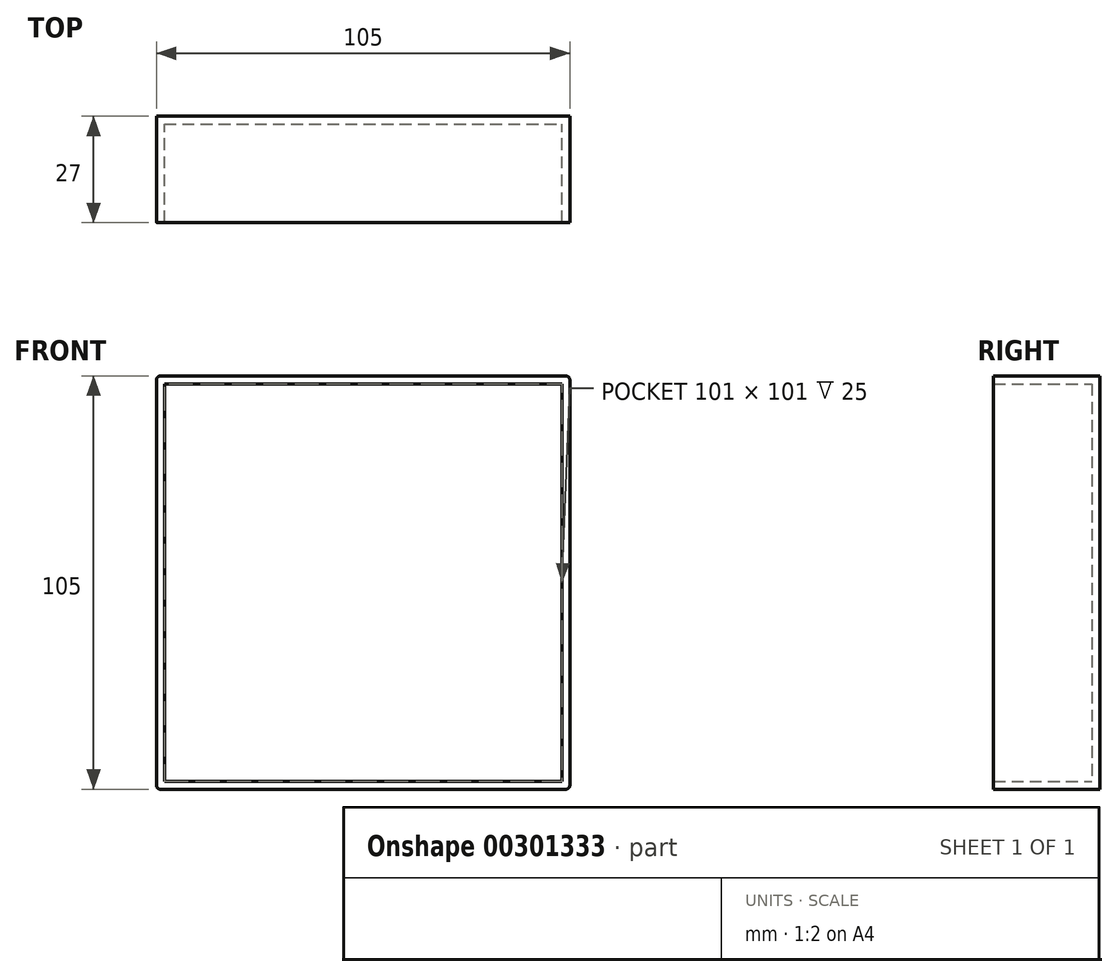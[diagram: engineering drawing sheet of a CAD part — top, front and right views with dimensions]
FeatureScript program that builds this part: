
annotation { "Feature Type Name" : "Feature", "Feature Type Description" : "" }
export const myFeature = defineFeature(function(context is Context, id is Id, definition is map)
    precondition{}
    {
        {
            var Q0;
            Q0=qCreatedBy(makeId("Front.planeOp"),FACE);
            var sketch = newSketch(context, id + "F0", { "sketchPlane" : qUnion([Q0])});
            skLineSegment(sketch, "E0.bottom", {"start": v(-37.92, 57.9) * mm, "end": v(67.08, 57.9) * mm});
            skLineSegment(sketch, "E0.top", {"start": v(-37.92, -47.1) * mm, "end": v(67.08, -47.1) * mm});
            skLineSegment(sketch, "E0.left", {"start": v(-37.92, 57.9) * mm, "end": v(-37.92, -47.1) * mm});
            skLineSegment(sketch, "E0.right", {"start": v(67.08, 57.9) * mm, "end": v(67.08, -47.1) * mm});
            skSolve(sketch);
        }
        {
            var Q0;
            Q0=makeQuery(id+"F0.imprint","IMPRINT",FACE,{"disambiguationData":[TD([[makeQuery(id+"F0.imprint","IMPRINT",EDGE,{"derivedFrom":sQuery(id+"F0.wireOp",EDGE,"E0.bottom")}),-1.0]])]});
            extrude(context, id + "F1", {"entities" : qUnion([Q0]), "depth" : 27 * mm});
        }
        {
            var Q0;
            Q0=makeQuery(id+"F1.opExtrude","CAP_FACE",FACE,{"disambiguationData":[OSD([sQuery(id+"F0.wireOp",EDGE,"E0.bottom"),sQuery(id+"F0.wireOp",EDGE,"E0.top"),sQuery(id+"F0.wireOp",EDGE,"E0.left"),sQuery(id+"F0.wireOp",EDGE,"E0.right")])],"isStart":false});
            shell(context, id + "F2", {"entities" : qUnion([Q0]), "thickness" : 2 * mm});
        }
        {
            var Q0;
            Q0=makeQuery(id+"F1.opExtrude","SWEPT_EDGE",EDGE,{"disambiguationData":[OSD([sQuery(id+"F0.wireOp",EDGE,"E0.bottom"),sQuery(id+"F0.wireOp",EDGE,"E0.right")])]});
            var Q1;
            Q1=makeQuery(id+"F1.opExtrude","SWEPT_EDGE",EDGE,{"disambiguationData":[OSD([sQuery(id+"F0.wireOp",EDGE,"E0.top"),sQuery(id+"F0.wireOp",EDGE,"E0.right")])]});
            var Q2;
            Q2=makeQuery(id+"F1.opExtrude","SWEPT_EDGE",EDGE,{"disambiguationData":[OSD([sQuery(id+"F0.wireOp",EDGE,"E0.bottom"),sQuery(id+"F0.wireOp",EDGE,"E0.left")])]});
            var Q3;
            Q3=makeQuery(id+"F1.opExtrude","SWEPT_EDGE",EDGE,{"disambiguationData":[OSD([sQuery(id+"F0.wireOp",EDGE,"E0.top"),sQuery(id+"F0.wireOp",EDGE,"E0.left")])]});
            fillet(context, id + "F3", {"entities" : qUnion([Q0, Q1, Q2, Q3]), "radius" : 1 * mm, "tangentPropagation" : true, "allowEdgeOverflow" : false});
        }
    });
